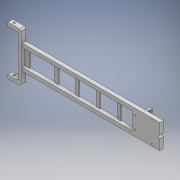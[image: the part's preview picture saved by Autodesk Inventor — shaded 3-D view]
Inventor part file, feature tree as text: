
AUTODESK INVENTOR PART (.ipt)
format: ipt  version: 2018 (Build 220112000, 112)  size: 414,720 bytes
history: native  units: mm
features: sketch x30, extrude x23, fillet x6, hole x5
ambient origin geometry x8: Origin, YZ Plane, XZ Plane, XY Plane, X Axis, Y Axis, Z Axis, Center Point
bodies: Solid1 (feature_tree)
feature tree (64):
  extrude  "Extrusion1"  Depth=50.0mm
  hole  "Hole1"  [1 undecoded]
  hole  "Hole2"  [1 undecoded]
  extrude  "Extrusion2"  Depth=25.0mm
  extrude  "Extrusion3"  Depth=25.0mm
  extrude  "Extrusion4"  Depth=5.0mm
  sketch  "Sketch7"  dims[d25=10.0mm d26=5.0mm]
  extrude  "Extrusion5"  Depth=5.0mm
  extrude  "Extrusion6"  Depth=35.0mm
  extrude  "Extrusion7"  Depth=35.0mm
  extrude  "Extrusion8"  Depth=35.0mm
  extrude  "Extrusion9"  Depth=2.0mm TaperAngle=0.0deg
  extrude  "Extrusion10"  Depth=7.5mm TaperAngle=0.0deg
  extrude  "Extrusion11"  Depth=10.0mm
  extrude  "Extrusion12"  Depth=7.5mm
  fillet  "Fillet1"  Radius=7.5mm
  fillet  "Fillet2"  Radius=25.0mm
  fillet  "Fillet3"  Radius=3.0mm
  fillet  "Fillet4"  Radius=3.2mm
  fillet  "Fillet5"  Radius=2.1mm
  fillet  "Fillet6"  Radius=5.5mm
  extrude  "Extrusion13"  Depth=92.5mm TaperAngle=0.0deg
  sketch  "Sketch17"  dims[d58=4.25mm d59=241.0mm d60=0.0mm]
  hole  "Hole3"  [1 undecoded]
  hole  "Hole4"  [1 undecoded]
  extrude  "Extrusion14"  Depth=5.0mm
  extrude  "Extrusion15"  Depth=2.5mm TaperAngle=0.0deg
  extrude  "Extrusion16"  Depth=30.0mm
  extrude  "Extrusion17"  Depth=2.5mm
  extrude  "Extrusion18"  Depth=14.55mm TaperAngle=0.0deg
  extrude  "Extrusion19"  Depth=0.1mm
  extrude  "Extrusion20"  Depth=3.25mm
  extrude  "Extrusion21"  Depth=3.25mm
  hole  "Hole5"  [1 undecoded]
  extrude  "Extrusion22"  Depth=2.0mm
  extrude  "Extrusion23"  Depth=7.5mm
  sketch  "Sketch1"  dims[d0=50.0mm d1=50.0mm]
  sketch  "Sketch2"  dims[d2=240.0mm d3=7.5mm]
  sketch  "Sketch3"  dims[d4=7.5mm d5=7.5mm d6=0.0mm]
  sketch  "Sketch4"  dims[d7=6.35mm d8=6.0mm d9=4.0mm d10=2.0mm d11=90.0deg d12=8.0mm d13=20.594885mm d14=25.0mm]
  sketch  "Sketch5"  dims[d15=3.3mm d16=6.0mm d17=4.0mm d18=2.0mm d19=90.0deg d20=8.0mm d21=20.594885mm d22=25.0mm]
  sketch  "Sketch6"  dims[d23=180.0deg d24=5.0mm]
  sketch  "Sketch8"  dims[d27=17.5mm d28=0.0mm d30=35.0mm]
  sketch  "Sketch9"  dims[d31=35.0mm d32=35.0mm]
  sketch  "Sketch10"  dims[d33=35.0mm d34=35.0mm]
  sketch  "Sketch11"  dims[d35=35.0mm d36=2.0mm d37=0.0mm]
  sketch  "Sketch12"  dims[d38=10.0mm d39=7.5mm d40=0.0mm]
  sketch  "Sketch13"  dims[d41=100.0mm d42=10.0mm]
  sketch  "Sketch14"  dims[d43=7.5mm d44=0.0mm d45=7.5mm d46=7.5mm d47=25.0mm d48=0.0mm d49=3.0mm d50=3.2mm d51=2.1mm d52=5.5mm]
  sketch  "Sketch15"  dims[d53=3.3mm d54=92.5mm d55=0.0mm]
  sketch  "Sketch16"  dims[d56=5.5mm d57=3.3mm]
  sketch  "Sketch18"  dims[d61=4.44mm d62=5.0mm]
  sketch  "Sketch19"  dims[d63=2.5mm d64=91.25mm d65=0.0mm]
  sketch  "Sketch20"  dims[d66=30.0mm d67=6.35mm]
  sketch  "Sketch21"  dims[d68=3.8mm d69=0.0mm d70=2.5mm]
  sketch  "Sketch22"  dims[d71=14.55mm d72=0.0mm d73=14.55mm d74=0.0mm]
  sketch  "Sketch23"  dims[d75=0.1mm d76=0.1mm]
  sketch  "Sketch24"  dims[d77=3.25mm d78=3.25mm]
  sketch  "Sketch25"  dims[d79=3.25mm d80=3.25mm]
  sketch  "Sketch26"  dims[d81=35.0mm d82=10.0mm]
  sketch  "Sketch27"  dims[d83=2.0mm d84=0.0mm d85=3.6mm]
  sketch  "Sketch28"  dims[d86=3.6mm]
  sketch  "Sketch29"  dims[d87=3.3mm d88=6.0mm d89=4.0mm d90=2.0mm d91=90.0deg d92=15.0mm d93=20.594885mm]
  sketch  "Sketch30"  dims[d94=3.3mm d95=6.0mm d96=4.0mm d97=2.0mm d98=90.0deg d99=15.0mm d100=20.594885mm d101=6.0mm d102=20.0mm d103=0.0mm d104=10.0mm d105=0.0mm d106=2.0mm d107=0.0mm d108=4.0mm d109=100.0mm d110=0.0mm d111=100.0mm d112=0.0mm d113=5.0mm d114=2.0mm d115=0.0mm d116=3.3mm d117=3.3mm d118=3.3mm d119=3.3mm d120=2.0mm d121=0.0mm d122=5.5mm d123=0.0mm d124=3.3mm d125=6.0mm d126=4.0mm d127=2.0mm d128=90.0deg d129=8.0mm d130=20.594885mm d131=42.0mm d132=17.0mm d133=21.0mm d135=8.5mm d136=15.825mm d137=3.5mm d138=21.0mm d139=3.3mm d140=3.3mm d141=3.3mm d142=10.0mm d143=0.0mm d144=7.5mm d145=0.0mm]
note: 5 required parameter values undecoded (feature->parameter linkage not recoverable at this tier; creation-order binding heuristic only, values carry confidence <= 0.55)
